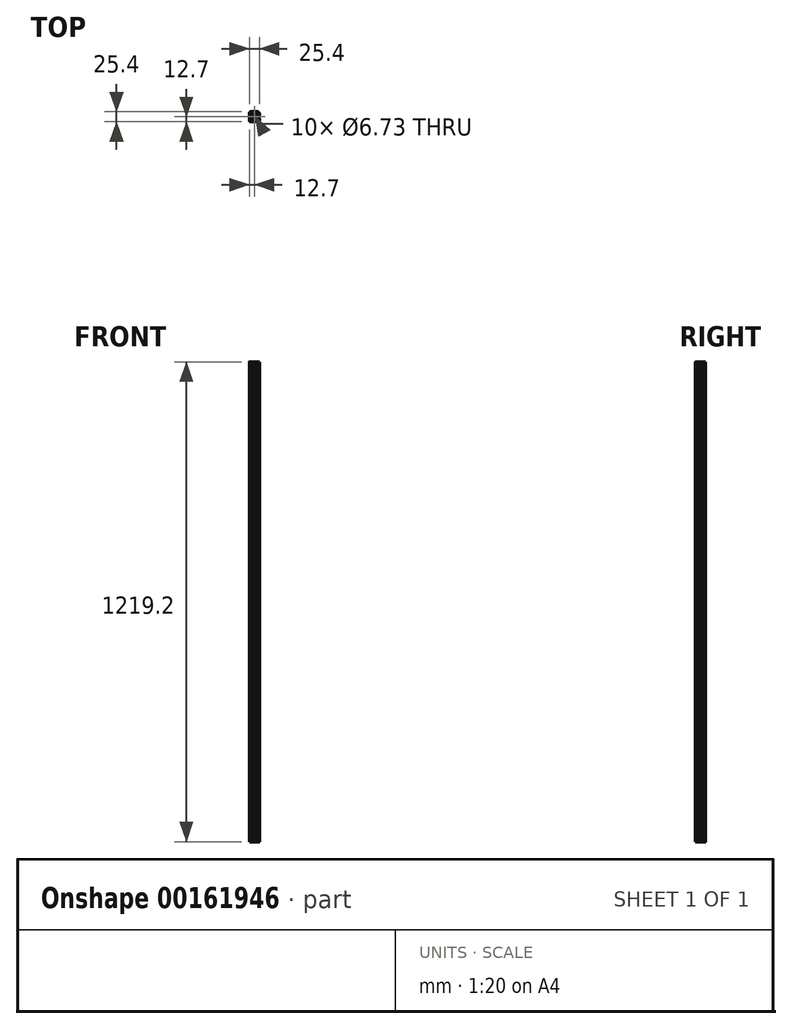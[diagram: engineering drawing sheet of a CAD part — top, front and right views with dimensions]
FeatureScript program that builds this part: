
annotation { "Feature Type Name" : "Feature", "Feature Type Description" : "" }
export const myFeature = defineFeature(function(context is Context, id is Id, definition is map)
    precondition{}
    {
        {
            var Q0;
            Q0=qCreatedBy(makeId("Top.planeOp"),FACE);
            var sketch = newSketch(context, id + "F0", { "sketchPlane" : qUnion([Q0])});
            skCircle(sketch, "E0", {"center": v(-12.7, 12.7) * mm, "radius": 3.36 * mm});
            skLineSegment(sketch, "E1.bottom", {"start": v(-11.24, 17.64) * mm, "end": v(-14.16, 17.64) * mm});
            skLineSegment(sketch, "E1.top", {"start": v(-11.24, 7.76) * mm, "end": v(-14.16, 7.76) * mm});
            skLineSegment(sketch, "E1.left", {"start": v(-7.76, 14.16) * mm, "end": v(-7.76, 11.24) * mm});
            skLineSegment(sketch, "E1.right", {"start": v(-17.64, 14.16) * mm, "end": v(-17.64, 11.24) * mm});
            skPoint(sketch, "E2.visualSharp", {"position": v(-25.4, 25.4) * mm});
            skPoint(sketch, "E3.visualSharp", {"position": v(0, 25.4) * mm});
            skPoint(sketch, "E4.visualSharp", {"position": v(0, 0) * mm});
            skPoint(sketch, "E5.visualSharp", {"position": v(-25.4, 0) * mm});
            skLineSegment(sketch, "E6.0", {"start": v(-18.7, 20.6) * mm, "end": v(-16.85, 18.76) * mm});
            skLineSegment(sketch, "E7.0", {"start": v(-20.6, 18.7) * mm, "end": v(-18.76, 16.85) * mm});
            skPoint(sketch, "E8.orphan", {"position": v(-23.85, 1.55) * mm});
            skPoint(sketch, "E9.orphan", {"position": v(-23.85, 23.85) * mm});
            skPoint(sketch, "E10.orphan", {"position": v(-1.55, 23.85) * mm});
            skPoint(sketch, "E11.orphan", {"position": v(-1.55, 1.55) * mm});
            skLineSegment(sketch, "E12", {"start": v(-8.55, 6.64) * mm, "end": v(-6.7, 4.8) * mm});
            skLineSegment(sketch, "E13.0", {"start": v(-18.7, 4.8) * mm, "end": v(-16.85, 6.64) * mm});
            skLineSegment(sketch, "E14.0", {"start": v(-20.6, 6.7) * mm, "end": v(-18.76, 8.55) * mm});
            skLineSegment(sketch, "E15.0", {"start": v(-8.55, 18.76) * mm, "end": v(-6.7, 20.6) * mm});
            skPoint(sketch, "E16.visualSharp", {"position": v(-23.85, 21.95) * mm});
            skArc(sketch, "E16.filletArc", {"start": v(-20.6, 18.7) * mm, "mid": v(-22.68, 19.1) * mm, "end": v(-23.85, 17.35) * mm});
            skPoint(sketch, "E17.visualSharp", {"position": v(-21.95, 23.85) * mm});
            skArc(sketch, "E17.filletArc", {"start": v(-17.35, 23.85) * mm, "mid": v(-19.1, 22.68) * mm, "end": v(-18.7, 20.6) * mm});
            skPoint(sketch, "E18.visualSharp", {"position": v(-5.34, 23.85) * mm});
            skLineSegment(sketch, "E19", {"start": v(-17.35, 23.85) * mm, "end": v(-15.58, 23.85) * mm});
            skLineSegment(sketch, "E20", {"start": v(-23.85, 17.35) * mm, "end": v(-23.85, 15.62) * mm});
            skLineSegment(sketch, "E21", {"start": v(-8.05, 1.55) * mm, "end": v(-9.78, 1.55) * mm});
            skArc(sketch, "E22.filletArc", {"start": v(-6.7, 20.6) * mm, "mid": v(-6.3, 22.68) * mm, "end": v(-8.05, 23.85) * mm});
            skPoint(sketch, "E23.visualSharp", {"position": v(-1.55, 3.45) * mm});
            skPoint(sketch, "E24.visualSharp", {"position": v(-3.45, 1.55) * mm});
            skArc(sketch, "E24.filletArc", {"start": v(-8.05, 1.55) * mm, "mid": v(-6.3, 2.73) * mm, "end": v(-6.7, 4.8) * mm});
            skArc(sketch, "E25.filletArc", {"start": v(-18.7, 4.8) * mm, "mid": v(-19.1, 2.73) * mm, "end": v(-17.35, 1.55) * mm});
            skArc(sketch, "E26.filletArc", {"start": v(-23.85, 8.05) * mm, "mid": v(-22.68, 6.3) * mm, "end": v(-20.6, 6.7) * mm});
            skLineSegment(sketch, "E27.bottom", {"start": v(-4.9, 0) * mm, "end": v(-8.05, 0) * mm});
            skLineSegment(sketch, "E27.top", {"start": v(-4.92, 25.4) * mm, "end": v(-8.05, 25.4) * mm});
            skLineSegment(sketch, "E27.left", {"start": v(0, 4.9) * mm, "end": v(0, 8.05) * mm});
            skLineSegment(sketch, "E27.right", {"start": v(-25.4, 4.9) * mm, "end": v(-25.4, 8.05) * mm});
            skArc(sketch, "E28.filletArc", {"start": v(-25.4, 3.81) * mm, "mid": v(-24.28, 1.12) * mm, "end": v(-21.59, 0) * mm});
            skArc(sketch, "E29.filletArc", {"start": v(-3.81, 0) * mm, "mid": v(-1.12, 1.12) * mm, "end": v(0, 3.8) * mm});
            skArc(sketch, "E30.filletArc", {"start": v(0, 21.59) * mm, "mid": v(-1.12, 24.28) * mm, "end": v(-3.8, 25.4) * mm});
            skArc(sketch, "E31.filletArc", {"start": v(-21.59, 25.4) * mm, "mid": v(-24.28, 24.28) * mm, "end": v(-25.4, 21.59) * mm});
            skPoint(sketch, "E32.newPointA", {"position": v(-17.64, 7.76) * mm});
            skArc(sketch, "E32.filletArc", {"start": v(-14.16, 7.76) * mm, "mid": v(-15.62, 7.47) * mm, "end": v(-16.85, 6.64) * mm});
            skPoint(sketch, "E33.newPointA", {"position": v(-7.76, 7.76) * mm});
            skArc(sketch, "E33.filletArc", {"start": v(-8.55, 6.64) * mm, "mid": v(-9.78, 7.47) * mm, "end": v(-11.24, 7.76) * mm});
            skArc(sketch, "E34.filletArc", {"start": v(-7.76, 11.24) * mm, "mid": v(-7.47, 9.78) * mm, "end": v(-6.64, 8.55) * mm});
            skArc(sketch, "E35.filletArc", {"start": v(-6.64, 16.85) * mm, "mid": v(-7.47, 15.62) * mm, "end": v(-7.76, 14.16) * mm});
            skPoint(sketch, "E36.newPointB", {"position": v(-7.76, 17.64) * mm});
            skArc(sketch, "E36.filletArc", {"start": v(-11.24, 17.64) * mm, "mid": v(-9.78, 17.93) * mm, "end": v(-8.55, 18.76) * mm});
            skPoint(sketch, "E37.newPointB", {"position": v(-17.64, 17.64) * mm});
            skArc(sketch, "E37.filletArc", {"start": v(-16.85, 18.76) * mm, "mid": v(-15.62, 17.93) * mm, "end": v(-14.16, 17.64) * mm});
            skArc(sketch, "E38.filletArc", {"start": v(-17.64, 14.16) * mm, "mid": v(-17.93, 15.62) * mm, "end": v(-18.76, 16.85) * mm});
            skArc(sketch, "E39.filletArc", {"start": v(-18.76, 8.55) * mm, "mid": v(-17.93, 9.78) * mm, "end": v(-17.64, 11.24) * mm});
            skLineSegment(sketch, "E40", {"start": v(-6.64, 8.55) * mm, "end": v(-4.8, 6.7) * mm});
            skPoint(sketch, "E41.visualSharp", {"position": v(-1.55, 21.95) * mm});
            skArc(sketch, "E42.filletArc", {"start": v(-4.8, 6.7) * mm, "mid": v(-2.73, 6.3) * mm, "end": v(-1.55, 8.05) * mm});
            skLineSegment(sketch, "E43", {"start": v(-1.55, 8.05) * mm, "end": v(-1.55, 9.78) * mm});
            skLineSegment(sketch, "E44", {"start": v(-6.64, 16.85) * mm, "end": v(-4.8, 18.7) * mm});
            skArc(sketch, "E45.filletArc", {"start": v(-1.55, 17.35) * mm, "mid": v(-2.73, 19.1) * mm, "end": v(-4.8, 18.7) * mm});
            skArc(sketch, "E46", {"start": v(-23.85, 9.78) * mm, "mid": v(-24.63, 10.56) * mm, "end": v(-25.4, 9.78) * mm});
            skArc(sketch, "E47", {"start": v(-25.4, 15.62) * mm, "mid": v(-24.63, 14.86) * mm, "end": v(-23.85, 15.62) * mm});
            skArc(sketch, "E48", {"start": v(-15.62, 23.85) * mm, "mid": v(-14.83, 24.63) * mm, "end": v(-15.62, 25.4) * mm});
            skArc(sketch, "E49", {"start": v(-9.78, 25.4) * mm, "mid": v(-10.6, 24.63) * mm, "end": v(-9.78, 23.85) * mm});
            skArc(sketch, "E50", {"start": v(-1.55, 15.62) * mm, "mid": v(-0.77, 14.88) * mm, "end": v(0, 15.62) * mm});
            skArc(sketch, "E51", {"start": v(0, 9.78) * mm, "mid": v(-0.77, 10.5) * mm, "end": v(-1.55, 9.78) * mm});
            skArc(sketch, "E52", {"start": v(-9.78, 1.55) * mm, "mid": v(-10.4, 0.77) * mm, "end": v(-9.78, 0) * mm});
            skArc(sketch, "E53", {"start": v(-15.62, 0) * mm, "mid": v(-14.85, 0.77) * mm, "end": v(-15.62, 1.55) * mm});
            skLineSegment(sketch, "E54.trimOffspring", {"start": v(-15.62, 1.55) * mm, "end": v(-17.35, 1.55) * mm});
            skLineSegment(sketch, "E55.trimOffspring", {"start": v(-16.7, 0) * mm, "end": v(-20.5, 0) * mm});
            skLineSegment(sketch, "E56.trimOffspring", {"start": v(-1.55, 15.62) * mm, "end": v(-1.55, 17.35) * mm});
            skLineSegment(sketch, "E57.trimOffspring", {"start": v(0, 15.62) * mm, "end": v(0, 16.26) * mm});
            skLineSegment(sketch, "E58.trimOffspring", {"start": v(-23.85, 9.78) * mm, "end": v(-23.85, 8.05) * mm});
            skLineSegment(sketch, "E59.trimOffspring", {"start": v(-25.4, 15.62) * mm, "end": v(-25.4, 16.26) * mm});
            skLineSegment(sketch, "E60.trimOffspring", {"start": v(-9.86, 23.85) * mm, "end": v(-8.05, 23.85) * mm});
            skLineSegment(sketch, "E61.trimOffspring", {"start": v(-15.58, 25.4) * mm, "end": v(-16.25, 25.4) * mm});
            skPoint(sketch, "E62.start.orphan", {"position": v(-15.62, 17.93) * mm});
            skPoint(sketch, "E63.start.orphan", {"position": v(-9.78, 17.93) * mm});
            skPoint(sketch, "E64.start.orphan", {"position": v(-7.47, 15.62) * mm});
            skPoint(sketch, "E65.start.orphan", {"position": v(-7.47, 9.78) * mm});
            skPoint(sketch, "E66.start.orphan", {"position": v(-17.93, 15.62) * mm});
            skPoint(sketch, "E67.start.orphan", {"position": v(-17.93, 9.78) * mm});
            skPoint(sketch, "E68.start.orphan", {"position": v(-9.78, 7.47) * mm});
            skPoint(sketch, "E69.start.orphan", {"position": v(-15.62, 7.47) * mm});
            skPoint(sketch, "E70.endSnap0", {"position": v(0, 18.6) * mm});
            skPoint(sketch, "E71.startSnap0", {"position": v(-1.55, 8.92) * mm});
            skArc(sketch, "E72", {"start": v(-4.92, 25.4) * mm, "mid": v(-4.37, 24.9) * mm, "end": v(-3.81, 25.4) * mm});
            skArc(sketch, "E73", {"start": v(-9.14, 25.4) * mm, "mid": v(-8.6, 24.86) * mm, "end": v(-8.05, 25.4) * mm});
            skArc(sketch, "E74", {"start": v(-17.35, 25.4) * mm, "mid": v(-16.8, 24.86) * mm, "end": v(-16.25, 25.4) * mm});
            skArc(sketch, "E75", {"start": v(-21.59, 25.4) * mm, "mid": v(-21.04, 24.85) * mm, "end": v(-20.49, 25.4) * mm});
            skLineSegment(sketch, "E76", {"start": v(-25.4, 21.59) * mm, "end": v(-25.4, 20.5) * mm});
            skArc(sketch, "E77", {"start": v(-25.4, 16.26) * mm, "mid": v(-24.84, 16.8) * mm, "end": v(-25.4, 17.35) * mm});
            skArc(sketch, "E78", {"start": v(-25.4, 8.05) * mm, "mid": v(-24.9, 8.6) * mm, "end": v(-25.4, 9.15) * mm});
            skArc(sketch, "E79", {"start": v(-25.4, 3.81) * mm, "mid": v(-24.85, 4.36) * mm, "end": v(-25.4, 4.9) * mm});
            skArc(sketch, "E80", {"start": v(-20.5, 0) * mm, "mid": v(-21.04, 0.55) * mm, "end": v(-21.59, 0) * mm});
            skArc(sketch, "E81", {"start": v(-15.62, 0) * mm, "mid": v(-16.16, 0.54) * mm, "end": v(-16.7, 0) * mm});
            skArc(sketch, "E82", {"start": v(-8.05, 0) * mm, "mid": v(-8.6, 0.55) * mm, "end": v(-9.15, 0) * mm});
            skArc(sketch, "E83", {"start": v(-3.81, 0) * mm, "mid": v(-4.35, 0.54) * mm, "end": v(-4.9, 0) * mm});
            skLineSegment(sketch, "E84.trimOffspring", {"start": v(-17.35, 25.4) * mm, "end": v(-20.49, 25.4) * mm});
            skLineSegment(sketch, "E85.trimOffspring", {"start": v(-25.4, 17.35) * mm, "end": v(-25.4, 21.59) * mm});
            skLineSegment(sketch, "E86.trimOffspring", {"start": v(-25.4, 9.15) * mm, "end": v(-25.4, 9.78) * mm});
            skLineSegment(sketch, "E87.trimOffspring", {"start": v(-9.15, 0) * mm, "end": v(-9.78, 0) * mm});
            skArc(sketch, "E88", {"start": v(0, 4.9) * mm, "mid": v(-0.54, 4.36) * mm, "end": v(0, 3.8) * mm});
            skArc(sketch, "E89", {"start": v(0, 9.15) * mm, "mid": v(-0.54, 8.6) * mm, "end": v(0, 8.05) * mm});
            skLineSegment(sketch, "E90.trimOffspring", {"start": v(0, 9.15) * mm, "end": v(0, 9.78) * mm});
            skArc(sketch, "E91", {"start": v(0, 21.59) * mm, "mid": v(-0.55, 21.04) * mm, "end": v(0, 20.5) * mm});
            skArc(sketch, "E92", {"start": v(0, 17.35) * mm, "mid": v(-0.55, 16.8) * mm, "end": v(0, 16.26) * mm});
            skLineSegment(sketch, "E93.trimOffspring", {"start": v(0, 17.35) * mm, "end": v(0, 20.5) * mm});
            skLineSegment(sketch, "E94.trimOffspring", {"start": v(-9.14, 25.4) * mm, "end": v(-9.86, 25.4) * mm});
            skSolve(sketch);
        }
        {
            var Q0;
            Q0=qSketchRegion(id+"F0",true);
            extrude(context, id + "F1", {"entities" : qUnion([Q0]), "depth" : 1219.2 * mm});
        }
    });
